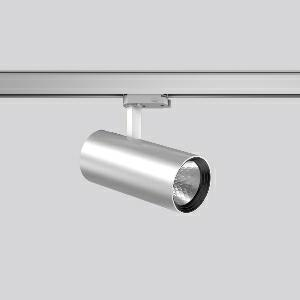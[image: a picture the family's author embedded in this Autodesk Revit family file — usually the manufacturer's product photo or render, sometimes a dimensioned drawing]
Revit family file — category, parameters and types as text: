
# Revit family: deecos_s_mini_742205_004_2_76_63e2
name_source: partatom
category: Lighting Fixtures
units: mm (PartAtom-declared; Revit-internal decimal feet)

## family parameters
Cut with Voids When Loaded = No
Host = Face
Light Source = No
Part Type = Normal
Room Calculation Point = No
Round Connector Dimension = Use Diameter
Shared = No

## types (1)
- DEECOS S mini (1 x LED Modul 927, 3500 lm, 2700)
    Apparent Load = 29 VA
    Approval mark = CE
    CIE Flux Codes = 95 99 100 100 100
    Color Rendering = 92
    Color Temperature = 2700
    Default Elevation = 1800 mm
    Description = Series: DEECOS S mini
LED surface-mounted projector in modern design with no visible cooling ribs. Housing: die-cast aluminium, powder-coated. Rotation range: 356°. Swivel range: 90°. Black plastic ring and recessed LED to prevent glare from the side. Optical assembly with reflector made of MIRO-Silver with 98% total light reflection for outstanding efficiency - can be changed without tools. Best colour rendering index Ra>90. With adapter for RZB 3-circuit DALI tracks. Suitable for Track on ceiling, Wall track. High quality converter without flickering and stroboscopic effect. The following accessories can be mounted without use of tools: interchangeable lenses, decorative glasses, honeycomb louvre, clear and frosted diffusers, white interchangeable plastic ring. 
Colour: silver
Diameter: 87 mm
Height: 214 mm
Lamp: LED
Socket: without socket
Colour temperature: 2700K
Colour rendering index (CRI): 92
System power: 29 W
Rated luminous flux: 3500 lm
Luminous efficiency: 121 lm/W
Control gear: Converter, dimmable, DALI
Protection class: I
Type of protection: IP 20
    Height = 214 mm
    Lamp = 1 x LED Modul 927
    Lamp Light Flux = 3500 lm
    Lamp count = 1
    Length = 87 mm
    Lifetime = 50000 h
    Luminous efficacy = 121 lm/W
    Manufacturer = RZB
    ModVariant = No
    Model = 742205.004.2.76
    Mounting Place = Ceiling
    Mounting Type = Rail mounted
    Number of Poles = 1
    OnlyDefault = Yes
    Power Factor = 1
    Product Name = DEECOS S mini
    Product group = Track mounted projectors
    ProductGroupID = 301
    Protection Class = Protection class I
    Protection Degree = IP 20
    RLX_Detail_Level = 1
    RLX_Emergency_Light_Flux = 0 lm
    RLX_Emergency_Type = 0
    RLX_Emergency_Type_DB = No
    RlxData = <blob elided: 37561 chars, md5=055a53aa>
    Socket = socket
    Standby Power = 0 W
    System Light Flux = 3500 lm
    System Power = 29 W
    Type Comments = Product without accessories
    Type Image = 741926.004.jpg
    URL = http://relux.com
    VarID = ---
    Voltage = 230 V
    Voltage Range = 220-240 V
    Weight = 0.00 kg
    Width = 0 mm  [stored 0 ft]

note: [stored X ft] marks values corroborated as IEEE doubles in the binary element streams (Revit-internal decimal feet)

## geometry (parser evidence)
native form markers: Blend x4, Sweep x12
no freeform markers — native parametric forms only
